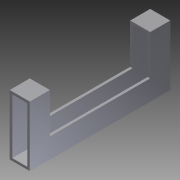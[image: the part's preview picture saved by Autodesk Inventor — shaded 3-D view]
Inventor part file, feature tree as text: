
AUTODESK INVENTOR PART (.ipt)
format: ipt  version: 2012 (Build 160160000, 160)  size: 94,720 bytes
history: native  units: in
note: dims shown in document units (in); Inventor stores cm internally (conversion verified against a paired STEP export)
features: extrude x2, sketch x2
ambient origin geometry x8: Origin, YZ Plane, XZ Plane, XY Plane, X Axis, Y Axis, Z Axis, Center Point
bodies: Solid1 (feature_tree)
feature tree (4):
  extrude  "Extrusion1"  Depth=1.0in
  extrude  "Extrusion2"  Depth=0.125in
  sketch  "Sketch1"  dims[d0=3.0in d1=1.0in]
  sketch  "Sketch2"  dims[d2=0.125in d3=0.125in d4=0.125in d5=0.125in d6=7.0in d7=0.0in d8=2.0in d9=1.0in d10=1.0in d11=7.0in d12=0.0in]
